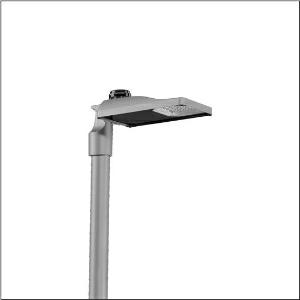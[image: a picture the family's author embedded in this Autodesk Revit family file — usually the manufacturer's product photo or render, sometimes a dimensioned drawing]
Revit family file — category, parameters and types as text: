
# Revit family: streetlight_sl_31_micro___p1_0a_5xh1a7bn08da_f975
name_source: partatom
category: Lighting Fixtures
units: mm (PartAtom-declared; Revit-internal decimal feet)

## family parameters
Cut with Voids When Loaded = No
Host = Face
Light Source = No
Part Type = Normal
Room Calculation Point = No
Round Connector Dimension = Use Diameter
Shared = No

## types (1)
- --- (1 x LED, 3700 lm, 35.5 W, 2200K)
    Apparent Load = 36 VA
    CIE Flux Codes = 23 55 94 100 100
    Color Rendering = 70
    Color Temperature = 2200K
    Default Elevation = 1800 mm
    Description = Streetlight SL 31 micro NEMA (7pin) mast luminaire for post-top, side-entry; light control with lens of PMMA; light distribution: P1.0a, direct asymmetric distribution, for standard-compliant lighting for roads and squares; LED: luminous flux: 3.700lm, light colour: 722, colour temperature: 2200K; luminous efficacy: 104,2lm/W; control: overheat protection, intelligent temperature release in ECG and LED module, constant luminous flux control, time-dependent luminous flux control, flexible luminous flux parameterisation, pre-setting: linear dimming characteristic; luminaire housing, of diecast aluminium, SITECO metallic grey (DB 702S), corrosivity category C5 high according to DIN EN ISO 12944; cover of toughened safety glass, transparent, mast flange of diecast aluminium, SITECO metallic grey (DB 702S), spigot size: 76/60mm, mast flange included unmounted; cable length: 6,5m, connection cable pre-assembled; mains connection: 220..240V, AC, 50/60Hz; power consumption (at start of service life): 35,5W / (at end of service life): 37,5W / (with reduced operation 50%): 15,4W; protection rating (complete): IP66; insulation class (complete): insulation class I (protective earthing); impact resistance: IK10; certification: CE, ENEC, ENEC+, VDE, UKCA; permissible operating ambient temperature for outdoor applications: -40..+50°C; packaging unit: 1 piece

Light Distribution: P1.0a
    Height = 76 mm
    Lamp = 1 x LED
    Lamp Light Flux = 3700 lm
    Lamp Power = 35.5 W
    Lamp count = 1
    Length = 467 mm
    Luminous efficacy = 104 lm/W
    Manufacturer = Siteco
    ModVariant = No
    Model = 5XH1A7BN08DA
    Mounting Place = Pole
    Mounting Type = Pole top
    Number of Poles = 1
    OnlyDefault = Yes
    Power Factor = 1
    Product Name = Streetlight SL 31 micro | P1.0a
    Product group = mast luminaire | pylon top
    ProductGroupID = 6100
    Protection Class = Protection class I
    Protection Degree = IP 66
    RLX_Detail_Level = 1
    RLX_Emergency_Light_Flux = 0 lm
    RLX_Emergency_Type = 0
    RLX_Emergency_Type_DB = No
    RlxData = <blob elided: 23309 chars, md5=9e505d77>
    Socket = socket
    Standby Power = 0 W
    System Light Flux = 3700 lm
    System Power = 36 W
    Type Comments = factory setting: luminous flux: 100 % | dim-lin: 254 | 700 mA
    Type Image = l_1300305.jpg
    URL = http://relux.com
    VarID = @adj_017005
    Voltage = 0 V
    Weight = 0.00 kg
    Width = 265 mm

## geometry (parser evidence)
native form markers: Blend x4, Sweep x9
no freeform markers — native parametric forms only
